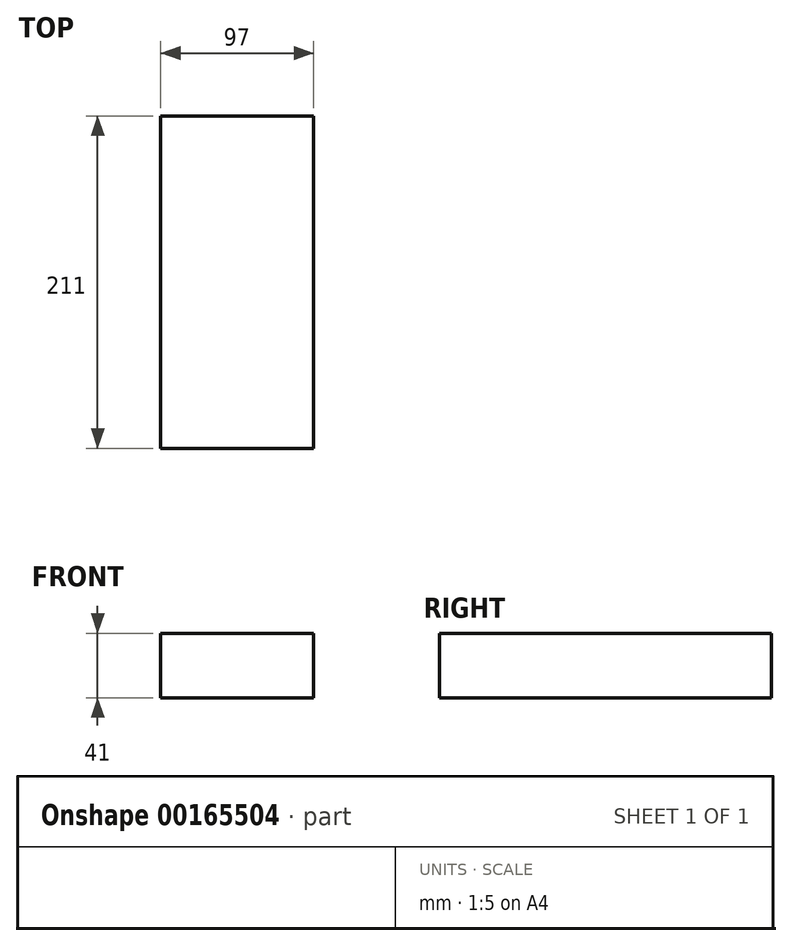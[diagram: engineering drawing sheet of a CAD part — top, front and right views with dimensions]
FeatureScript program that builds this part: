
annotation { "Feature Type Name" : "Feature", "Feature Type Description" : "" }
export const myFeature = defineFeature(function(context is Context, id is Id, definition is map)
    precondition{}
    {
        {
            var Q0;
            Q0=qCreatedBy(makeId("Top.planeOp"),FACE);
            var sketch = newSketch(context, id + "F0", { "sketchPlane" : qUnion([Q0])});
            skLineSegment(sketch, "E0.bottom", {"start": v(48.5, -105.5) * mm, "end": v(-48.5, -105.5) * mm});
            skLineSegment(sketch, "E0.top", {"start": v(48.5, 105.5) * mm, "end": v(-48.5, 105.5) * mm});
            skLineSegment(sketch, "E0.left", {"start": v(48.5, -105.5) * mm, "end": v(48.5, 105.5) * mm});
            skLineSegment(sketch, "E0.right", {"start": v(-48.5, -105.5) * mm, "end": v(-48.5, 105.5) * mm});
            skPoint(sketch, "E0.middle", {"position": v(0, 0) * mm});
            skSolve(sketch);
        }
        {
            var Q0;
            Q0 = qSketchRegion(id + "F0", true);
            extrude(context, id + "F1", {"entities" : qUnion([Q0]), "depth" : 41 * mm});
        }
    });
